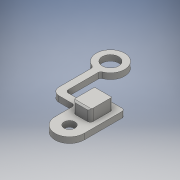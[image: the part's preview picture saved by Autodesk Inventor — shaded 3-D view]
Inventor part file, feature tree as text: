
AUTODESK INVENTOR PART (.ipt)
format: ipt  version: 2016 (Build 200138000, 138)  size: 1,034,240 bytes
history: native  units: mm
features: other x37, extrude x32, fillet x11, sketch x7, chamfer x3, mirror x3, draft x2, hole x2
ambient origin geometry x8: Origin, YZ Plane, XZ Plane, XY Plane, X Axis, Y Axis, Z Axis, Center Point
bodies: Body1 (feature_tree), Body2 (feature_tree), Body3 (feature_tree), Body4 (feature_tree), Body5 (feature_tree), Body6 (feature_tree)
feature tree (97):
  other  "Table"
  other  "MyPart_V0_Cases_bare_minimum"
  other  "MyPart_V0_Cases_carabiner"
  other  "MyPart_V0_Cases_base_mount"
  other  "MyPart_V0_Cases_side_mount"
  other  "MyPart_V0_Cases_wire"
  other  "case"
  other  "case sketch"
  other  "case_meets_lid"
  other  "pcb_detail_sketch"
  extrude  "case bottom"  Depth=45.0mm
  extrude  "case sides"  Depth=0.5mm
  other  "battery_bot_channe_offset"
  extrude  "case standoff"  Depth=21.0mm TaperAngle=0.0deg
  extrude  "inlet cut"  Depth=1.1mm TaperAngle=0.0deg
  extrude  "outlet cut"  Depth=6.1mm
  extrude  "usb_opening"  Depth=1.1mm TaperAngle=0.0deg
  extrude  "fpc opening"  Depth=1.0mm
  extrude  "lid_extrude"  Depth=1.0mm
  extrude  "nub_for_switch"  TaperAngle=0.0deg  [1 undecoded]
  extrude  "baffles"  Depth=1.0mm
  extrude  "half_height_baffles"  Depth=1.0mm
  extrude  "usb_lower baffel"  TaperAngle=60.0deg  [1 undecoded]
  other  "tabs_sketch"
  other  "tab where"
  other  "tab_where_2"
  extrude  "tab out"  Depth=1.0mm
  extrude  "tab_on_case"  Depth=10.0mm TaperAngle=0.0deg
  chamfer  "Chamfer10"  [1 undecoded]
  fillet  "fillets_for_bottom"  Radius=25.307274mm
  fillet  "lid-fillets"  Radius=10.0mm
  fillet  "lid_pencil_fillets"  Radius=6.0mm
  other  "button sketch"
  extrude  "button base extrude"  Depth=1.0mm
  extrude  "button_to_exterior"  Depth=10.0mm
  chamfer  "button_chamfer"  Distance=1.6mm
  fillet  "button_fillets"  Radius=1.6mm
  extrude  "button_light_channel"  Depth=1.0mm
  extrude  "extrude hole pattern top'"  Depth=1.0mm
  extrude  "extrude hole pattern taper"  Depth=1.0mm
  other  "mounting pattern"
  extrude  "Mounting tabs"  Depth=1.0mm
  other  "countersink seat"
  extrude  "countersink"  Depth=1.0mm
  other  "midplane y"
  other  "midplane x"
  mirror  "mount mirror"
  mirror  "mount mirror 2"
  fillet  "fillet_basemount"  Radius=1.6mm
  other  "temp lid sketch"
  extrude  "Extrusion31"  Depth=1.0mm
  extrude  "Extrusion32"  Depth=1.0mm
  fillet  "Fillet14"  Radius=20.0mm
  extrude  "shim_extrusion_begin"  Depth=1.0mm
  extrude  "shim tab"  Depth=1.0mm
  chamfer  "slide in chamber for shim"  Distance=5.5mm
  other  "easy_in_for button_holder"
  extrude  "side mount extrude"  Depth=1.0mm
  draft  "FaceDraft4"
  draft  "FaceDraft5"
  hole  "counterbore hole 1"  [1 undecoded]
  hole  "counterbore hle1"  [1 undecoded]
  fillet  "sidemount fillets"  Radius=0.8mm
  extrude  "carabiner_extrude"  Depth=1.0mm
  other  "carabiner_draft"
  fillet  "carabiner_filles"  Radius=0.8mm
  extrude  "wire loop extrude"  Depth=1.0mm
  extrude  "wire loop extrude cut"  Depth=1.0mm
  mirror  "Mirror6"
  fillet  "wire loop fillet 0"  Radius=0.8mm
  fillet  "wire loop fillet 1"  Radius=0.8mm
  extrude  "cutout_for_screw_clearance"  Depth=1.0mm
  extrude  "Extrusion42"  Depth=1.0mm
  fillet  "extra fillets for screw clearance cutouts"  Radius=1.4mm
  extrude  "Extrusion45"  Depth=1.0mm TaperAngle=0.0deg
  other  "inlet sketch"
  other  "outlet sketc"
  other  "helper "
  other  "usb_cut_sketch"
  other  "lid_main"
  other  "lid"
  other  "tabs_on_body"
  other  "button"
  other  "light funnel"
  other  "temp_lid"
  other  "shim sketch"
  other  "shims"
  sketch  "Sketch24"  dims[d0=38.0mm d1=45.0mm]
  other  "fpc sketch"
  other  "side mount sketch"
  sketch  "Sketch27"  dims[d2=1.6mm d3=0.5mm]
  sketch  "Sketch28"  dims[d4=1.2mm d5=0.0mm d6=21.0mm d7=0.0mm]
  sketch  "Sketch29"  dims[d8=21.0mm d14=1.1mm d15=0.0mm]
  sketch  "Sketch30"  dims[d16=7.81mm d17=6.1mm]
  sketch  "Sketch31"  dims[d18=8.31mm d20=1.1mm d21=0.0mm]
  sketch  "Sketch32"  dims[d22=11.5mm d23=3.5mm d25=3.0mm d26=0.0mm d27=0.0mm d44=3.4mm d45=3.0mm d46=60.0deg d47=3.7mm d49=10.0mm d50=0.0mm d51=-10.0mm d52=25.307274mm d53=-4.0mm d54=10.0mm d55=0.0mm d56=6.0mm d148=5.0mm d149=10.0mm d166=1.6mm d167=1.6mm d168=1.6mm d169=1.6mm d170=22.5mm d171=2.5mm d172=3.5mm d173=1.6mm d174=1.6mm d175=1.6mm d176=1.6mm d177=20.0mm d178=3.5mm d179=1.8mm d180=5.5mm d181=1.0mm d182=19.0mm d183=10.0mm d184=0.0mm d185=0.8mm d186=0.8mm d187=0.8mm d188=0.8mm d189=0.8mm d192=0.8mm d193=0.8mm d195=21.08mm d196=0.4mm d197=1.4mm d198=0.0mm d199=3.8mm d200=0.0mm d205=0.8mm d221=3.0mm d222=4.0mm d223=2.5mm d227=0.8mm d228=1.4mm d229=0.0mm d236=1.3mm d237=0.0mm d238=4.0mm d240=0.5mm d241=0.8mm d242=0.75mm d243=2.0mm d244=1.0mm d245=0.4mm d251=24.89mm d252=9.14mm d253=13.21mm d254=1.5mm d256=2.5mm d257=0.8mm d261=1.0mm d262=0.0mm d263=2.0mm d264=0.0mm d267=1.9mm d269=0.5mm d270=0.7mm d271=2.5mm d272=2.0mm d273=-0.872665mm d274=0.8mm d276=0.8mm d278=1.3mm d279=0.25mm d280=2.0mm d281=45.0deg d285=0.5mm d286=2.0mm d287=9.5mm d288=0.2mm d289=2.0mm d290=10.0mm d291=0.0mm d292=2.36mm d293=0.0mm d294=2.0mm d295=1.5875mm d296=3.175mm d297=15.0mm d298=3.0mm d299=13.0mm d300=0.2mm d301=0.0mm d302=0.8mm d303=0.4mm d304=0.0mm d305=2.0mm d306=2.0mm d307=45.0deg d308=9.0mm d309=6.0mm d311=1.2mm d312=1.2mm d313=0.7mm d314=1.5mm d315=0.4mm d316=0.0mm d317=0.5mm d318=2.0mm d319=45.0deg d320=-0.5mm d322=0.8mm d323=28.7mm d324=7.0mm d325=4.0mm d326=0.8mm d327=10.0mm d328=0.0mm d329=0.2mm d330=1.0mm d331=0.349066mm d332=3.3mm d333=9.0mm d335=8.0mm d336=0.0mm d412=10.0mm d413=10.0mm d339=3.0mm d340=6.0mm d341=6.0mm d342=5.0mm d343=90.0deg d344=8.0mm d345=20.594885mm d414=10.0mm d415=10.0mm d348=3.0mm d349=6.0mm d350=6.0mm d351=5.0mm d352=90.0deg d353=8.0mm d354=20.594885mm d355=2.0mm d356=2.0mm d360=1.0mm d364=15.0mm d365=2.5mm d366=2.5mm d367=2.5mm d368=7.0mm d369=6.0mm d370=0.0mm d375=2.181662mm d376=2.5mm d377=5.0mm d378=2.5mm d379=1.0mm d380=1.5mm d381=6.108652mm d382=35.0mm d383=10.0mm d384=2.5mm d385=1.5875mm d387=2.5mm d388=30.0deg d389=4.0mm d390=2.5mm d391=0.0mm d392=25.0mm d393=35.0mm d394=2.5mm d395=0.0mm d401=2.0mm d402=5.0mm d403=1.0mm d404=2.0mm d407=5.0mm d408=5.0mm d409=3.490659mm d410=3.490659mm d411=4.3mm d416=2.0mm d417=0.8mm d420=23.0mm d421=0.8mm d424=1.6mm d426=4.1mm d430=2.0mm d431=2.0mm d432=0.0mm d433=4.0mm d434=14.3mm d436=2.0mm d437=2.5mm d438=2.0mm d439=6.0mm d440=0.1mm d441=0.1mm d443=4.0mm d444=1.5mm d445=0.0mm d446=0.5mm d447=4.3mm d448=1.5mm d449=0.0mm d450=0.8mm d451=0.0mm d452=1.0mm d453=0.2mm d454=2.0mm d455=0.0mm]
  other  "button_poker"
note: 5 required parameter values undecoded (feature->parameter linkage not recoverable at this tier; creation-order binding heuristic only, values carry confidence <= 0.55)
